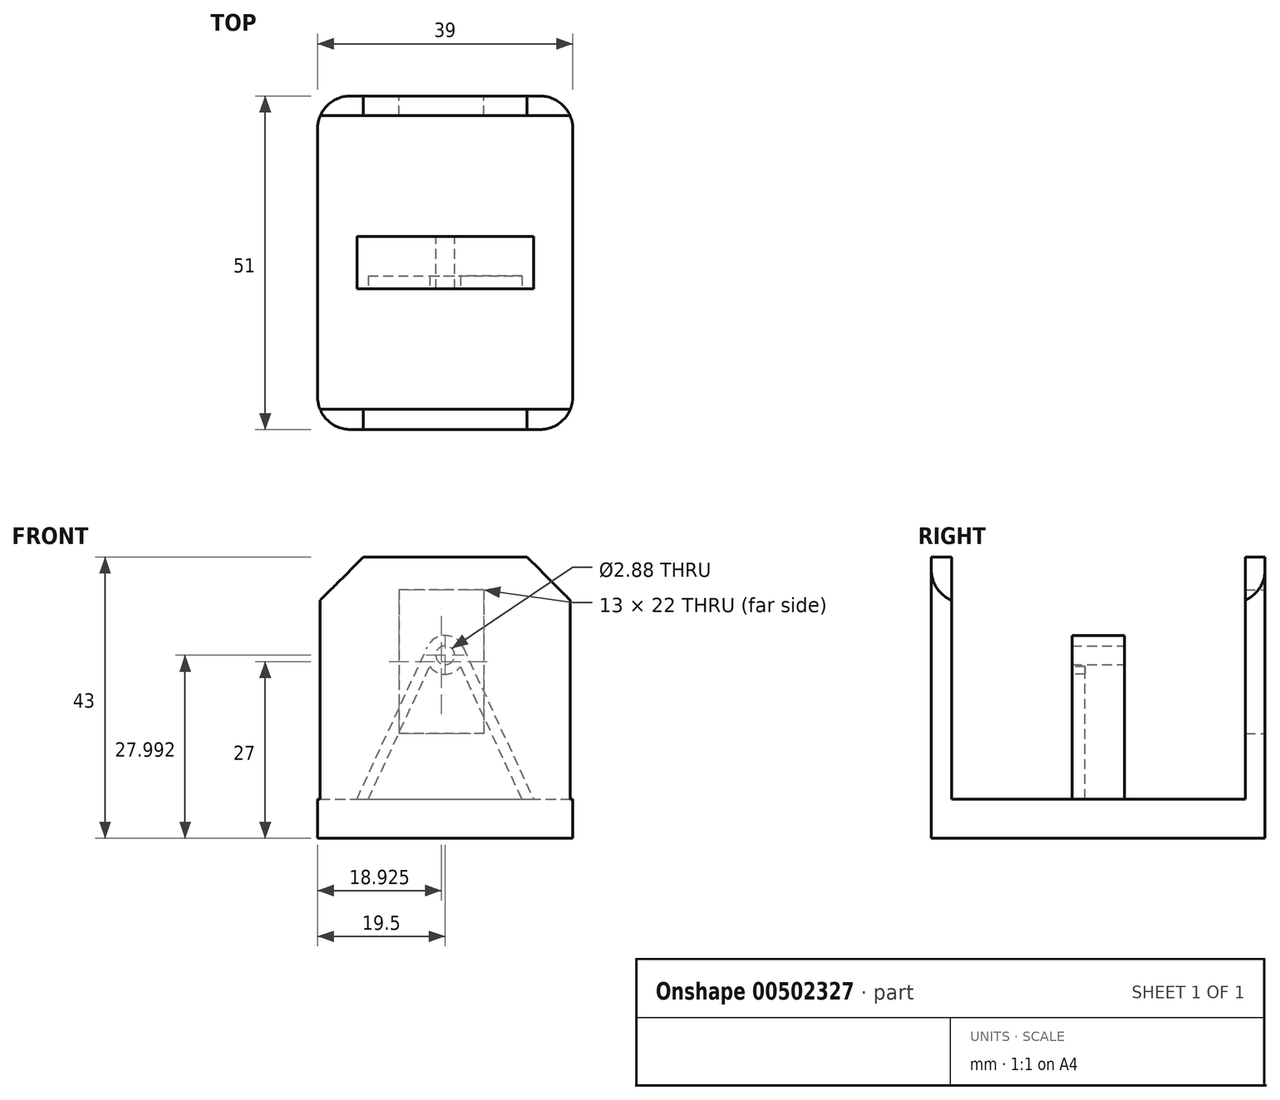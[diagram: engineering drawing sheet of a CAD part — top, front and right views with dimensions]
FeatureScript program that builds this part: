
annotation { "Feature Type Name" : "Feature", "Feature Type Description" : "" }
export const myFeature = defineFeature(function(context is Context, id is Id, definition is map)
    precondition{}
    {
        {
            var Q0;
            Q0=qCreatedBy(makeId("Top.planeOp"),FACE);
            var sketch = newSketch(context, id + "F0", { "sketchPlane" : qUnion([Q0])});
            skLineSegment(sketch, "E0.bottom", {"start": v(-19.5, 25.5) * mm, "end": v(19.5, 25.5) * mm});
            skLineSegment(sketch, "E0.top", {"start": v(-19.5, -25.5) * mm, "end": v(19.5, -25.5) * mm});
            skLineSegment(sketch, "E0.left", {"start": v(-19.5, 25.5) * mm, "end": v(-19.5, -25.5) * mm});
            skLineSegment(sketch, "E0.right", {"start": v(19.5, 25.5) * mm, "end": v(19.5, -25.5) * mm});
            skSolve(sketch);
        }
        {
            var Q0;
            Q0 = qSketchRegion(id + "F0", true);
            extrude(context, id + "F1", {"entities" : qUnion([Q0]), "depth" : 6 * mm});
        }
        {
            var Q0;
            Q0=qCreatedBy(makeId("Front.planeOp"),FACE);
            var sketch = newSketch(context, id + "F2", { "sketchPlane" : qUnion([Q0])});
            skLineSegment(sketch, "E1", {"start": v(-13.5, 6) * mm, "end": v(-2.72, 29.25) * mm});
            skLineSegment(sketch, "E2", {"start": v(2.72, 29.25) * mm, "end": v(13.5, 6) * mm});
            skPoint(sketch, "E3.visualSharp", {"position": v(0, 35.13) * mm});
            skArc(sketch, "E3.filletArc", {"start": v(2.72, 29.25) * mm, "mid": v(0, 31) * mm, "end": v(-2.72, 29.25) * mm});
            skCircle(sketch, "E4", {"center": v(0, 28) * mm, "radius": 1.44 * mm});
            skLineSegment(sketch, "E5", {"start": v(-13.5, 6) * mm, "end": v(13.5, 6) * mm});
            skSolve(sketch);
        }
        {
            var Q0;
            Q0 = qSketchRegion(id + "F2", true);
            extrude(context, id + "F3", {"entities" : qUnion([Q0]), "operationType" : NewBodyOperationType.ADD, "depth" : 4 * mm, "hasSecondDirection" : true, "secondDirectionOppositeDirection" : true, "secondDirectionDepth" : 4 * mm});
        }
        {
            var Q0;
            Q0=makeQuery(id+"F3.opExtrude","CAP_FACE",FACE,{"disambiguationData":[OSD([sQuery(id+"F2.wireOp",EDGE,"E1"),sQuery(id+"F2.wireOp",EDGE,"E2"),sQuery(id+"F2.wireOp",EDGE,"E3.filletArc"),sQuery(id+"F2.wireOp",EDGE,"E4"),sQuery(id+"F2.wireOp",EDGE,"E5")])],"isStart":false});
            var sketch = newSketch(context, id + "F4", { "sketchPlane" : qUnion([Q0])});
            skLineSegment(sketch, "E6", {"start": v(-11.75, 6) * mm, "end": v(-2.32, 26.34) * mm});
            skLineSegment(sketch, "E7", {"start": v(11.72, 6) * mm, "end": v(2.29, 26.34) * mm});
            skCircle(sketch, "E8", {"center": v(0, 28) * mm, "radius": 2.91 * mm});
            skSolve(sketch);
        }
        {
            var Q0;
            {var subQ0=sQuery(id+"F4.wireOp",EDGE,"E6");var subQ1=makeQuery(id+"F3.opExtrude","CAP_EDGE",EDGE,{"disambiguationData":[OSD([sQuery(id+"F2.wireOp",EDGE,"E5")])],"isStart":false});var subQ2=makeQuery(id+"F4.imprint","INTERSECT",VERTEX,{"derivedFrom":[subQ1,subQ0]});Q0=makeQuery(id+"F4.imprint","IMPRINT",FACE,{"disambiguationData":[TD([[makeQuery(id+"F4.imprint","IMPRINT",EDGE,{"disambiguationData":[TD([[subQ2,-1.0]])],"derivedFrom":subQ0}),-1.0]])]});}
            extrude(context, id + "F5", {"entities" : qUnion([Q0]), "operationType" : NewBodyOperationType.REMOVE, "oppositeDirection" : true, "depth" : 2 * mm});
        }
        {
            var Q0;
            {var subQ0=sQuery(id+"F2.wireOp",EDGE,"E5");Q0=makeQuery(id+"FbU6YqpNJ9WnbEs_1.1.F5.boolean.opBoolean","MERGE",FACE,{"derivedFrom":[makeQuery(id+"F5.boolean.opBoolean","MERGE",FACE,{"derivedFrom":[makeQuery(id+"F1.opExtrude","CAP_FACE",FACE,{"disambiguationData":[OSD([sQuery(id+"F0.wireOp",EDGE,"E0.bottom"),sQuery(id+"F0.wireOp",EDGE,"E0.top"),sQuery(id+"F0.wireOp",EDGE,"E0.left"),sQuery(id+"F0.wireOp",EDGE,"E0.right")])],"isStart":false}),makeQuery(id+"F5.opExtrude","SWEPT_FACE",FACE,{"disambiguationData":[OSD([subQ0])]})]}),makeQuery(id+"FbU6YqpNJ9WnbEs_1.1.F5.opExtrude","SWEPT_FACE",FACE,{"disambiguationData":[OSD([subQ0])]})]});}
            var sketch = newSketch(context, id + "F6", { "sketchPlane" : qUnion([Q0])});
            skLineSegment(sketch, "E9", {"start": v(-19.5, 25.5) * mm, "end": v(-19.5, 22.52) * mm});
            skLineSegment(sketch, "E10", {"start": v(-19.5, 22.52) * mm, "end": v(19.5, 22.52) * mm});
            skLineSegment(sketch, "E11", {"start": v(19.5, 22.52) * mm, "end": v(19.5, 25.5) * mm});
            skLineSegment(sketch, "E12", {"start": v(19.5, 25.5) * mm, "end": v(-19.5, 25.5) * mm});
            skLineSegment(sketch, "E13", {"start": v(-19.5, -25.5) * mm, "end": v(-19.5, -22.38) * mm});
            skLineSegment(sketch, "E14", {"start": v(-19.5, -22.38) * mm, "end": v(19.5, -22.38) * mm});
            skLineSegment(sketch, "E15", {"start": v(19.5, -22.38) * mm, "end": v(19.5, -25.5) * mm});
            skLineSegment(sketch, "E16", {"start": v(19.5, -25.5) * mm, "end": v(-19.5, -25.5) * mm});
            skSolve(sketch);
        }
        {
            var Q0;
            Q0 = qSketchRegion(id + "F6", true);
            extrude(context, id + "F7", {"entities" : qUnion([Q0]), "operationType" : NewBodyOperationType.ADD, "depth" : 37 * mm});
        }
        {
            var Q0;
            Q0=makeQuery(id+"F7.opExtrude","CAP_EDGE",EDGE,{"disambiguationData":[OSD([sQuery(id+"F6.wireOp",EDGE,"E11")])],"isStart":false});
            var Q1;
            Q1=makeQuery(id+"F7.opExtrude","CAP_EDGE",EDGE,{"disambiguationData":[OSD([sQuery(id+"F6.wireOp",EDGE,"E9")])],"isStart":false});
            var Q2;
            Q2=makeQuery(id+"F7.opExtrude","CAP_EDGE",EDGE,{"disambiguationData":[OSD([sQuery(id+"F6.wireOp",EDGE,"E13")])],"isStart":false});
            var Q3;
            Q3=makeQuery(id+"F7.opExtrude","CAP_EDGE",EDGE,{"disambiguationData":[OSD([sQuery(id+"F6.wireOp",EDGE,"E15")])],"isStart":false});
            chamfer(context, id + "F8", {"entities" : qUnion([Q0, Q1, Q2, Q3]), "width" : 7 * mm, "tangentPropagation" : true});
        }
        {
            var Q0;
            Q0=makeQuery(id+"F7.boolean.opBoolean","MERGE",EDGE,{"derivedFrom":[makeQuery(id+"F1.opExtrude","SWEPT_EDGE",EDGE,{"disambiguationData":[OSD([sQuery(id+"F0.wireOp",EDGE,"E0.top"),sQuery(id+"F0.wireOp",EDGE,"E0.right")])]}),makeQuery(id+"F7.opExtrude","SWEPT_EDGE",EDGE,{"disambiguationData":[OSD([sQuery(id+"F6.wireOp",EDGE,"E15"),sQuery(id+"F6.wireOp",EDGE,"E16")])]})]});
            var Q1;
            Q1=makeQuery(id+"F7.boolean.opBoolean","MERGE",EDGE,{"derivedFrom":[makeQuery(id+"F1.opExtrude","SWEPT_EDGE",EDGE,{"disambiguationData":[OSD([sQuery(id+"F0.wireOp",EDGE,"E0.top"),sQuery(id+"F0.wireOp",EDGE,"E0.left")])]}),makeQuery(id+"F7.opExtrude","SWEPT_EDGE",EDGE,{"disambiguationData":[OSD([sQuery(id+"F6.wireOp",EDGE,"E13"),sQuery(id+"F6.wireOp",EDGE,"E16")])]})]});
            var Q2;
            Q2=makeQuery(id+"F7.boolean.opBoolean","MERGE",EDGE,{"derivedFrom":[makeQuery(id+"F1.opExtrude","SWEPT_EDGE",EDGE,{"disambiguationData":[OSD([sQuery(id+"F0.wireOp",EDGE,"E0.bottom"),sQuery(id+"F0.wireOp",EDGE,"E0.right")])]}),makeQuery(id+"F7.opExtrude","SWEPT_EDGE",EDGE,{"disambiguationData":[OSD([sQuery(id+"F6.wireOp",EDGE,"E11"),sQuery(id+"F6.wireOp",EDGE,"E12")])]})]});
            var Q3;
            Q3=makeQuery(id+"F7.boolean.opBoolean","MERGE",EDGE,{"derivedFrom":[makeQuery(id+"F1.opExtrude","SWEPT_EDGE",EDGE,{"disambiguationData":[OSD([sQuery(id+"F0.wireOp",EDGE,"E0.bottom"),sQuery(id+"F0.wireOp",EDGE,"E0.left")])]}),makeQuery(id+"F7.opExtrude","SWEPT_EDGE",EDGE,{"disambiguationData":[OSD([sQuery(id+"F6.wireOp",EDGE,"E9"),sQuery(id+"F6.wireOp",EDGE,"E12")])]})]});
            fillet(context, id + "F9", {"entities" : qUnion([Q0, Q1, Q2, Q3]), "radius" : 5 * mm, "tangentPropagation" : true, "allowEdgeOverflow" : false});
        }
        {
            var Q0;
            Q0=makeQuery(id+"F7.boolean.opBoolean","MERGE",FACE,{"derivedFrom":[makeQuery(id+"F1.opExtrude","SWEPT_FACE",FACE,{"disambiguationData":[OSD([sQuery(id+"F0.wireOp",EDGE,"E0.bottom")])]}),makeQuery(id+"F7.opExtrude","SWEPT_FACE",FACE,{"disambiguationData":[OSD([sQuery(id+"F6.wireOp",EDGE,"E12")])]})]});
            var sketch = newSketch(context, id + "F10", { "sketchPlane" : qUnion([Q0])});
            skLineSegment(sketch, "E17.bottom", {"start": v(-5.92, 38) * mm, "end": v(7.08, 38) * mm});
            skLineSegment(sketch, "E17.top", {"start": v(-5.92, 16) * mm, "end": v(7.08, 16) * mm});
            skLineSegment(sketch, "E17.left", {"start": v(-5.92, 38) * mm, "end": v(-5.92, 16) * mm});
            skLineSegment(sketch, "E17.right", {"start": v(7.08, 38) * mm, "end": v(7.08, 16) * mm});
            skSolve(sketch);
        }
        {
            var Q0;
            Q0=makeQuery(id+"F10.imprint","IMPRINT",FACE,{"disambiguationData":[TD([[makeQuery(id+"F10.imprint","IMPRINT",EDGE,{"derivedFrom":sQuery(id+"F10.wireOp",EDGE,"E17.bottom")}),-1.0]])]});
            extrude(context, id + "F11", {"entities" : qUnion([Q0]), "operationType" : NewBodyOperationType.REMOVE, "oppositeDirection" : true, "depth" : 15.8 * mm});
        }
    });
